# Revit family: PMS-PENDANT-Round
name_source: partatom
category: Lighting Fixtures
revit_build: Autodesk Revit 2014 (Build: 20130308_1515(x64)
units: mm (PartAtom-declared; Revit-internal decimal feet)

## types (1)
- ACRD-Pendant Mount
    Apparent Load = 42 VA
    Backbox = Paint - Hubbell - Green Textured
    Default Elevation = 48"
    Description = The Arts & Crafts® family of fixtures reflect the style and warmth of the Craftsman era. These fixtures are available in two sizes for post, wall or pendant mounting, as well as a matching bollard. The Arts & Crafts refractor system includes a symmetric and an asymmetric pattern to help control glare, while a wide variety of shade materials and finishes provides customization.
    Features = Full cutoff, dark sky compliant optical
system with solid shade
• Low angle beam has a maximum
candlepower at 65° for efficient spacing
between fixtures and control of glare
• Translucent shades add visual interest
when illuminated
• Pole, wall, and pendant mounting options
    Glass = Hubbell- White Glass
    Lamp = Compact Fluorecent/Metal Halide/Electronic Metal Halide/Pulse Start Metal Halide/High Pressure Sodium
    Manufacturer = Architectural Area Lighting
    Model = ACRD-Pendant Mount
    Nominal Watts = 42 W
    Product Documentation Link = https://hubbellcdn.com
    Product Page URL = https://www.hubbell.com
    URL = https://www.hubbell.com
    Voltage = 120 V
    Wattage Comments = 26,32 or 42 W

## geometry (parser evidence)
native form markers: Blend x14, Sweep x4
no freeform markers — native parametric forms only
